# Revit family: SILVER LED EMERGENCY EXIT LIGHT TWT6851WK
name_source: partatom
category: Electrical Fixtures
revit_build: Autodesk Revit 2015 (Build: 20160512_0715(x64)
units: mm (PartAtom-declared; Revit-internal decimal feet)

## types (4) — shared parameters
Depth = 84 mm  [stored 0.275591 ft]
Height = 209 mm  [stored 0.685696 ft]
Manufacturer = Teknoware Oy
Model = SILVER 68
Product Code = TWT6851WK
Viewing Distance = 30000 mm
Width = 412 mm  [stored 1.35171 ft]

## per-type parameters (varying)
| type | Back Pictogram | Down | Front Pictogram | Left | Right | Type Comments | Up |
| -arrow right | Teknoware Pictogram PBV3003 right back | No | Teknoware Pictogram PBV3003 right front | No | Yes | PBV3003 | No |
| -arrow left | Teknoware Pictogram PBV3003 left back | No | Teknoware Pictogram PBV3003 left front | Yes | No | PBV3003 | No |
| -arrow down | Teknoware Pictogram PBV3002 back | Yes | Teknoware Pictogram PBV3002 front | No | No | PBV3002 | No |
| -arrow up | Teknoware Pictogram PBV3005 back | No | Teknoware Pictogram PBV3005 front | No | No | PBV3005 | Yes |

note: [stored X ft] marks values corroborated as IEEE doubles in the binary element streams (Revit-internal decimal feet)

## geometry (parser evidence)
native form markers: Blend x10, Sweep x16
no freeform markers — native parametric forms only
